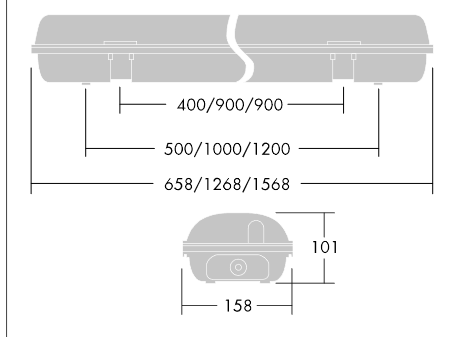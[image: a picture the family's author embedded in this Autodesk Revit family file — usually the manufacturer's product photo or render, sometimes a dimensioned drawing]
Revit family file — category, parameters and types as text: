
# Revit family: CBE_SURFACE MOUNTED LUMINAIRE LED
name_source: partatom
category: Luminaires
units: mm (PartAtom-declared; Revit-internal decimal feet)

## family parameters
Cote de connecteur circulaire = Utiliser le diamètre
Couper avec des vides une fois chargée = Non
Hôte = Face
Numéro OmniClass = 23.80.70.11
Partagée = Non
Point de calcul de pièce = Non
Source d'éclairage = Non
Titre OmniClass = Luminaries for Internal Lighting
Type d'élément = Normal

## types (2) — shared parameters
Body = Thorn_Metal_Light_Grey
Charge apparente = 45 VA
Code d'assemblage = D5020200
Cover = Thorn_PMMA_Semitransparent
Description = LED surface mount luminaire
Fabricant = Thorn Lighting
Lampe = LED
Modèle = 96545191
URL = www.thornlighting.com/96545191
Voltage = 230 V
zero-valued in all types: Elévation par défaut

## type names (no varying parameters)
- POSEIDON L1200
- POSEIDON L1200 2

## geometry (parser evidence)
native form markers: Blend x2, Sweep x3
no freeform markers — native parametric forms only
